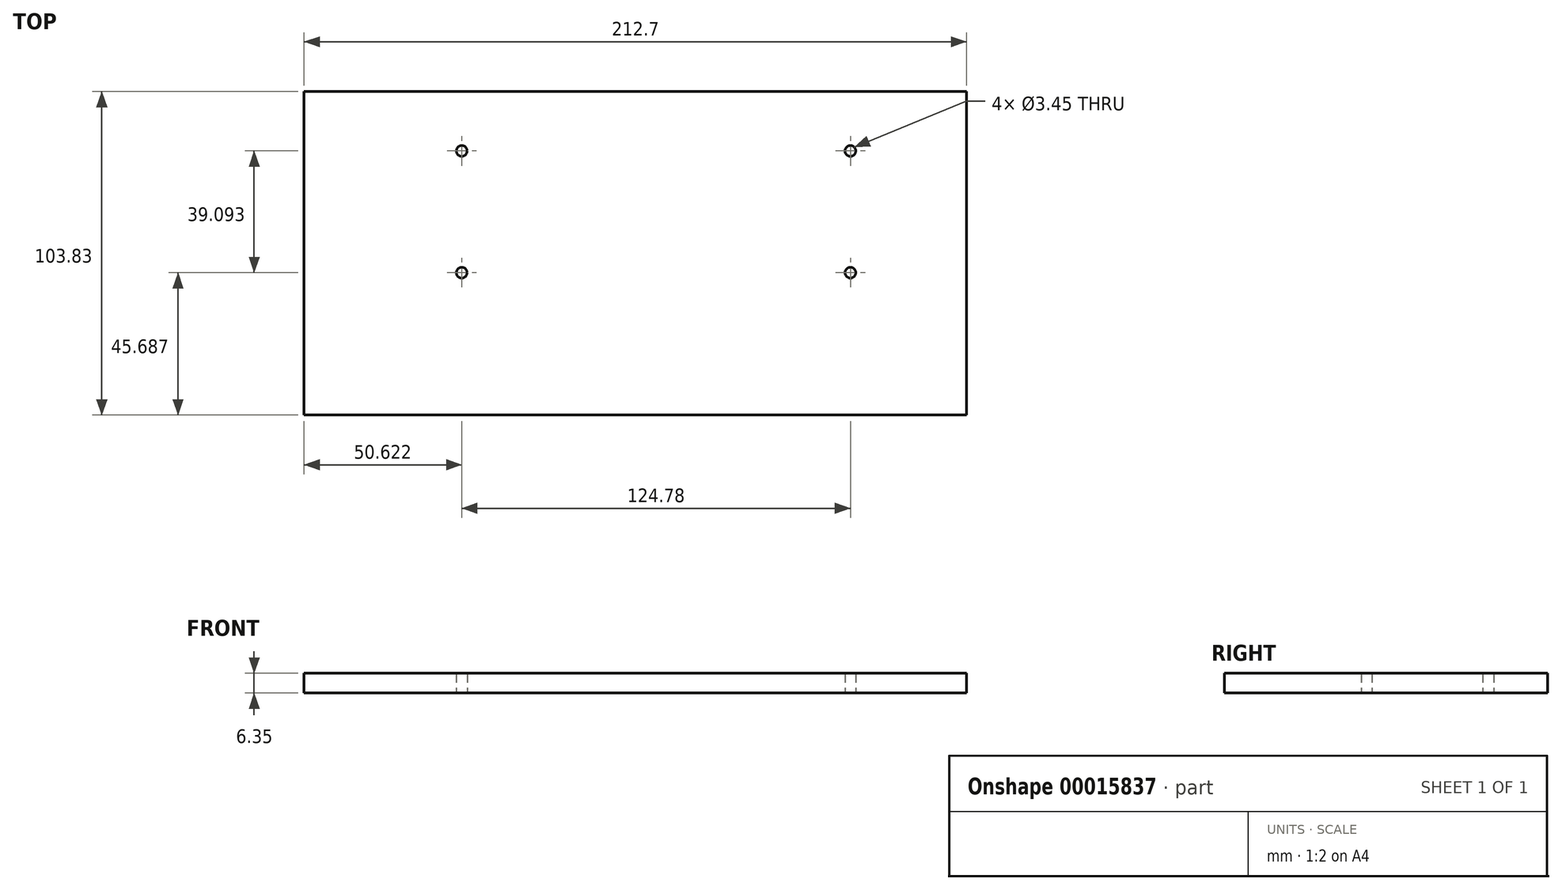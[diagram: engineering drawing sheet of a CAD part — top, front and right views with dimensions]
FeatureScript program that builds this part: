
annotation { "Feature Type Name" : "Feature", "Feature Type Description" : "" }
export const myFeature = defineFeature(function(context is Context, id is Id, definition is map)
    precondition{}
    {
        {
            var Q0;
            Q0=qCreatedBy(makeId("Top.planeOp"),FACE);
            var sketch = newSketch(context, id + "F0", { "sketchPlane" : qUnion([Q0])});
            skLineSegment(sketch, "E0.bottom", {"start": v(0, 0) * mm, "end": v(212.7, 0) * mm});
            skLineSegment(sketch, "E0.top", {"start": v(0, -103.83) * mm, "end": v(212.7, -103.83) * mm});
            skLineSegment(sketch, "E0.left", {"start": v(0, 0) * mm, "end": v(0, -103.83) * mm});
            skLineSegment(sketch, "E0.right", {"start": v(212.7, 0) * mm, "end": v(212.7, -103.83) * mm});
            skLineSegment(sketch, "E1", {"start": v(50.62, 0) * mm, "end": v(50.62, -19.05) * mm});
            skLineSegment(sketch, "E2", {"start": v(50.62, -19.05) * mm, "end": v(50.62, -58.14) * mm});
            skLineSegment(sketch, "E3", {"start": v(175.4, 0) * mm, "end": v(175.4, -19.05) * mm});
            skLineSegment(sketch, "E4", {"start": v(175.4, -19.05) * mm, "end": v(175.4, -58.14) * mm});
            skCircle(sketch, "E5", {"center": v(50.62, -19.05) * mm, "radius": 1.73 * mm});
            skCircle(sketch, "E6", {"center": v(50.62, -58.14) * mm, "radius": 1.73 * mm});
            skCircle(sketch, "E7", {"center": v(175.4, -58.14) * mm, "radius": 1.73 * mm});
            skCircle(sketch, "E8", {"center": v(175.4, -19.05) * mm, "radius": 1.73 * mm});
            skLineSegment(sketch, "E9", {"start": v(0, -51.92) * mm, "end": v(19.05, -51.92) * mm});
            skLineSegment(sketch, "E10", {"start": v(19.05, -51.92) * mm, "end": v(33.92, -51.92) * mm});
            skLineSegment(sketch, "E11", {"start": v(212.7, -51.92) * mm, "end": v(193.65, -51.92) * mm});
            skLineSegment(sketch, "E12", {"start": v(193.65, -51.92) * mm, "end": v(140.31, -51.92) * mm});
            skSolve(sketch);
        }
        {
            var Q0;
            Q0 = qSketchRegion(id + "F0", true);
            extrude(context, id + "F1", {"entities" : qUnion([Q0]), "depth" : 6.35 * mm});
        }
    });
